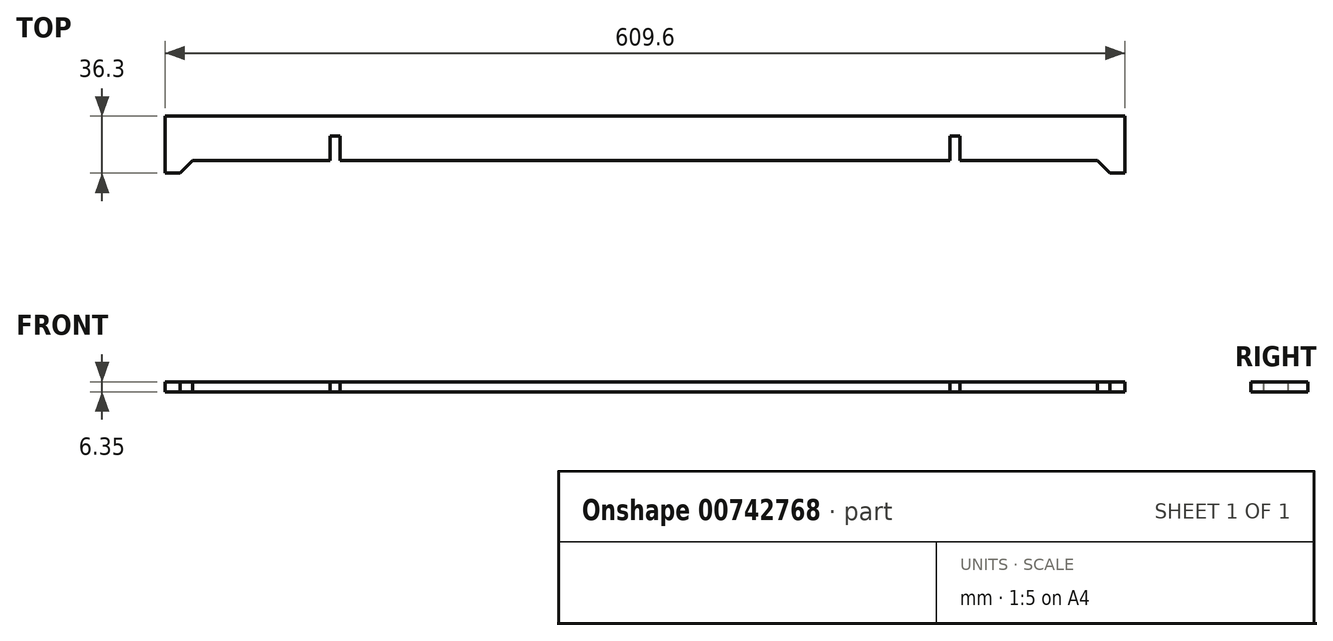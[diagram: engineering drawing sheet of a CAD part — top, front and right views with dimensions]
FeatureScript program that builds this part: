
annotation { "Feature Type Name" : "Feature", "Feature Type Description" : "" }
export const myFeature = defineFeature(function(context is Context, id is Id, definition is map)
    precondition{}
    {
        {
            var Q0;
            Q0=qCreatedBy(makeId("Top.planeOp"),FACE);
            var sketch = newSketch(context, id + "F0", { "sketchPlane" : qUnion([Q0])});
            skLineSegment(sketch, "E0.0", {"start": v(31.75, 138.11) * mm, "end": v(641.35, 138.11) * mm});
            skLineSegment(sketch, "E1.0", {"start": v(136.53, 109.74) * mm, "end": v(136.53, 125.41) * mm});
            skLineSegment(sketch, "E2.0", {"start": v(142.88, 109.74) * mm, "end": v(142.88, 125.41) * mm});
            skLineSegment(sketch, "E3.0", {"start": v(536.58, 109.74) * mm, "end": v(536.58, 125.41) * mm});
            skLineSegment(sketch, "E4.0", {"start": v(530.23, 109.74) * mm, "end": v(530.23, 125.41) * mm});
            skLineSegment(sketch, "E5.0", {"start": v(31.75, 101.8) * mm, "end": v(41.27, 101.8) * mm});
            skLineSegment(sketch, "E6.0", {"start": v(631.83, 101.8) * mm, "end": v(641.35, 101.8) * mm});
            skLineSegment(sketch, "E7.0", {"start": v(641.35, 101.8) * mm, "end": v(641.35, 138.11) * mm});
            skLineSegment(sketch, "E8.0", {"start": v(31.75, 101.8) * mm, "end": v(31.75, 138.11) * mm});
            skLineSegment(sketch, "E9.0", {"start": v(49.21, 109.74) * mm, "end": v(136.53, 109.74) * mm});
            skLineSegment(sketch, "E10", {"start": v(631.83, 101.8) * mm, "end": v(623.89, 109.74) * mm});
            skLineSegment(sketch, "E11", {"start": v(41.27, 101.8) * mm, "end": v(49.21, 109.74) * mm});
            skLineSegment(sketch, "E12.trimOffspring", {"start": v(142.88, 109.74) * mm, "end": v(530.23, 109.74) * mm});
            skLineSegment(sketch, "E13.trimOffspring", {"start": v(536.58, 109.74) * mm, "end": v(623.89, 109.74) * mm});
            skLineSegment(sketch, "E14.0", {"start": v(136.53, 125.41) * mm, "end": v(142.88, 125.41) * mm});
            skLineSegment(sketch, "E15.trimOffspring", {"start": v(530.23, 125.41) * mm, "end": v(536.58, 125.41) * mm});
            skSolve(sketch);
        }
        {
            var Q0;
            Q0=qSketchRegion(id+"F0",true);
            extrude(context, id + "F1", {"entities" : qUnion([Q0]), "depth" : 6.35 * mm, "offsetDistance" : 25.4 * mm});
        }
    });
